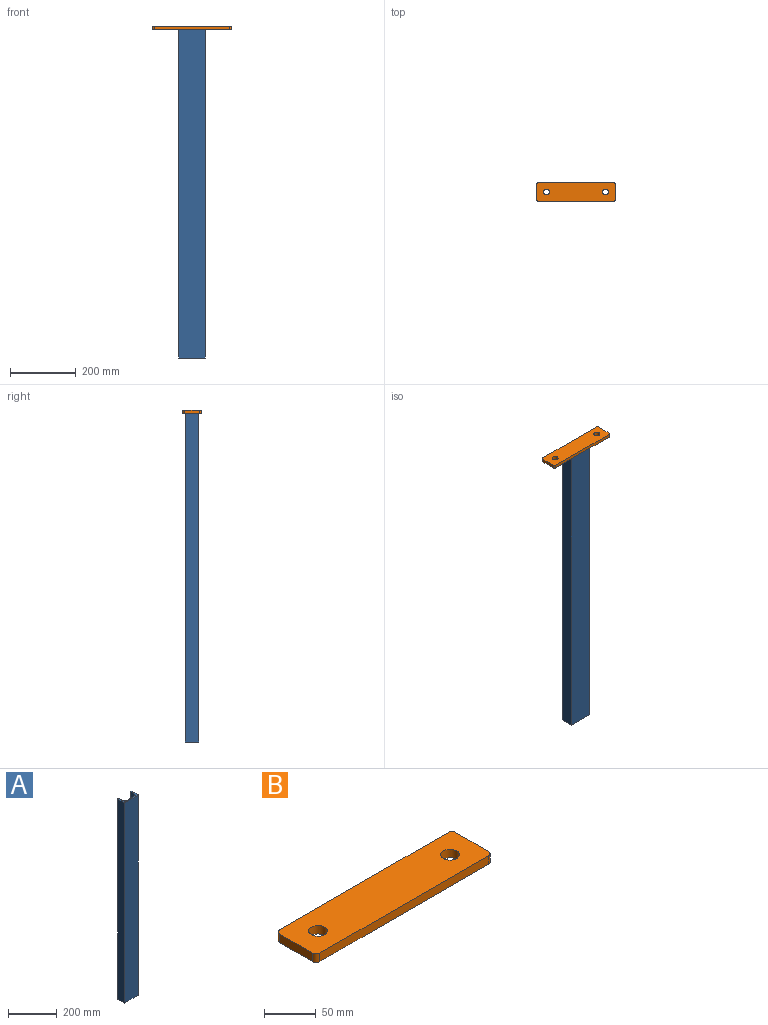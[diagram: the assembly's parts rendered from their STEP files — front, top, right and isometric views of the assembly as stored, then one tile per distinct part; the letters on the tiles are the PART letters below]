
ASSEMBLY  parts=2 mates=1
PART A: 14 faces, bbox 80x40x1000 mm
  f0: plane 1000x22.96mm, normal (1,0.08,0), area 23030.3mm2, adj f8,f9,f10,f13
  f1: plane 1000x2.71mm, normal (0,1,0), area 2707.2mm2, adj f2,f8,f9,f10
  f2: plane 1000x40mm, normal (-1,0,0), area 40000mm2, adj f1,f3,f8,f9
  f3: plane 1000x80mm, normal (0,-1,0), area 80000mm2, adj f2,f4,f8,f9
  f4: plane 1000x40mm, normal (1,0,0), area 40000mm2, adj f3,f5,f8,f9
  f5: plane 1000x2.71mm, normal (0,1,0), area 2707.2mm2, adj f4,f8,f9,f11
  f6: plane 1000x22.96mm, normal (-1,0.08,0), area 23030.3mm2, adj f8,f9,f11,f12
  f7: plane 1000x46.99mm, normal (0,1,0), area 46988.9mm2, adj f8,f9,f12,f13
  f8: plane 80x40mm, normal (0,0,-1), area 1024.7mm2, adj f0,f1,f2,f3,f4,f5,f6,f7
  f9: plane 80x40mm, normal (0,0,1), area 1024.7mm2, adj f0,f1,f2,f3,f4,f5,f6,f7
  f10: cylinder r=4mm len=1000mm, axis (0,0,1), area 5963.9mm2, adj f0,f1,f8,f9
  f11: cylinder r=4mm len=1000mm, axis (0,0,-1), area 5963.9mm2, adj f5,f6,f8,f9
  f12: cylinder r=8mm len=1000mm, axis (0,0,1), area 11927.7mm2, adj f6,f7,f8,f9
  f13: cylinder r=8mm len=1000mm, axis (0,0,-1), area 11927.7mm2, adj f0,f7,f8,f9
PART B: 12 faces, bbox 240x55x10 mm
  f0: plane 230x10mm, normal (0,1,0), area 2300mm2, adj f4,f5,f8,f11
  f1: plane 45x10mm, normal (-1,0,0), area 450mm2, adj f4,f5,f8,f9
  f2: plane 230x10mm, normal (0,-1,0), area 2300mm2, adj f4,f5,f9,f10
  f3: plane 45x10mm, normal (1,0,0), area 450mm2, adj f4,f5,f10,f11
  f4: plane 240x55mm, normal (0,0,1), area 12669.6mm2, adj f0,f1,f2,f3,f6,f7,f8,f9
  f5: plane 240x55mm, normal (0,0,-1), area 12669.6mm2, adj f0,f1,f2,f3,f6,f7,f8,f9
  f6: cylinder r=9mm len=18mm, axis (0,0,1), area 565.5mm2, adj f4,f5
  f7: cylinder r=9mm len=18mm, axis (0,0,1), area 565.5mm2, adj f4,f5
  f8: cylinder r=5mm len=10mm, axis (0,0,-1), area 78.5mm2, adj f0,f1,f4,f5
  f9: cylinder r=5mm len=10mm, axis (0,0,1), area 78.5mm2, adj f1,f2,f4,f5
  f10: cylinder r=5mm len=10mm, axis (0,0,-1), area 78.5mm2, adj f2,f3,f4,f5
  f11: cylinder r=5mm len=10mm, axis (0,0,1), area 78.5mm2, adj f0,f3,f4,f5
PLACE A t=(-266.98,-301.92,312.08)mm fixed
PLACE B t=(-266.98,-301.73,312.08)mm
MATE fastened B.f5 <-> A.f9  axis (0,0,-1) through (-266.98,-301.73,312.08)mm
